# Revit family: QF_MACOM_KM-550MAJ
name_source: partatom
category: Specialty Equipment
units: mm (PartAtom-declared; Revit-internal decimal feet)

## family parameters
Always vertical = Yes
Cut with Voids When Loaded = No
OmniClass Number = 23.40.40.14.27
OmniClass Title = Ice Machines
Part Type = Normal
Room Calculation Point = No
Round Connector Dimension = Use Diameter
Shared = No
Work Plane-Based = No

## types (1)
- KM-550MAJ
    Apparent Power = 0 VA
    Cold Water Connection Height = 775 mm
    Cold Water Consumption = 0
    Cold Water Flow = 0,0 L/s
    Cold Water Maximum Pressure = 0,0 Pa
    Cold Water Minimum Pressure = 0,0 Pa
    Cold Water RI Height = 0 mm
    Cold Water Size = 1/2"
    Cold Water Temperature Recommended = 0 °C
    Conn Conduit = Yes
    Default Elevation = 0 mm
    Description = MAQUINA DE GELO EM CUBO MACOM, SEM DEPOSITO - 220V 60HZ PL. N
    Elec Conn RI Height = 0 mm
    FL Amps = 0 A
    Indirect Waste Connection Height = 31 mm
    Indirect Waste Flow = 0,0 L/s
    Indirect Waste Size = 1"
    Manufacturer = MACOM
    Max Overcurrent Protection = 0 A
    Min Ckt Ampacity = 0 A
    Model = KM-550MAJ
    Number of Poles = 0
    Production per Cycle = 960 ice cubes
    Room Temperature = 0
    Storage = B-362I or B-226I
    Volume = 0,44 m³
    Waste Water Discharge Temperature = 0 °C

## geometry (parser evidence)
native form markers: Blend x11, Sweep x6
no freeform markers — native parametric forms only
